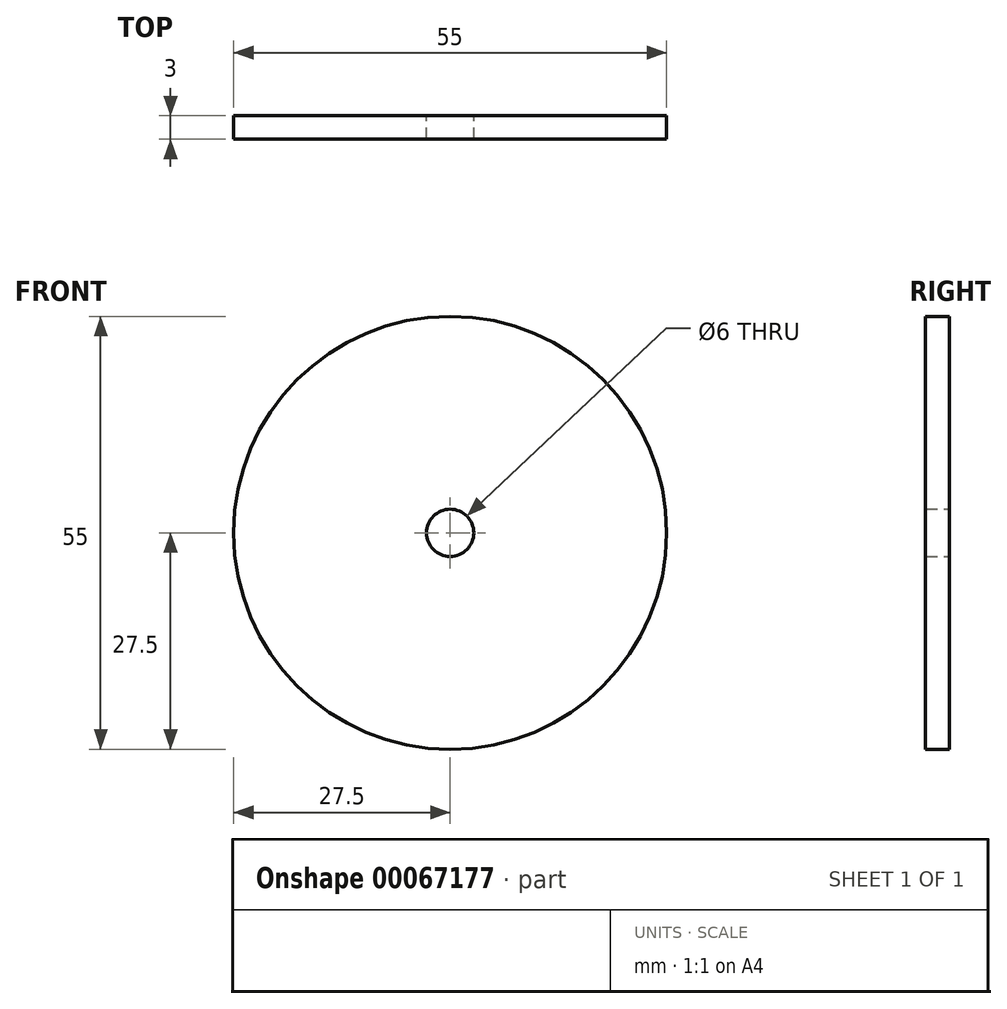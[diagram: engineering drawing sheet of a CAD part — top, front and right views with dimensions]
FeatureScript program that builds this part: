
annotation { "Feature Type Name" : "Feature", "Feature Type Description" : "" }
export const myFeature = defineFeature(function(context is Context, id is Id, definition is map)
    precondition{}
    {
        {
            var Q0;
            Q0=qCreatedBy(makeId("Front.planeOp"),FACE);
            var sketch = newSketch(context, id + "F0", { "sketchPlane" : qUnion([Q0])});
            skCircle(sketch, "E0", {"center": v(0, 0) * mm, "radius": 3 * mm});
            skCircle(sketch, "E1", {"center": v(0, 0) * mm, "radius": 27.5 * mm});
            skSolve(sketch);
        }
        {
            var Q0;
            Q0=makeQuery(id+"F0.imprint","IMPRINT",FACE,{"disambiguationData":[TD([[makeQuery(id+"F0.imprint","IMPRINT",EDGE,{"derivedFrom":sQuery(id+"F0.wireOp",EDGE,"E0")}),-1.0]])]});
            extrude(context, id + "F1", {"entities" : qUnion([Q0]), "depth" : 3 * mm});
        }
    });
